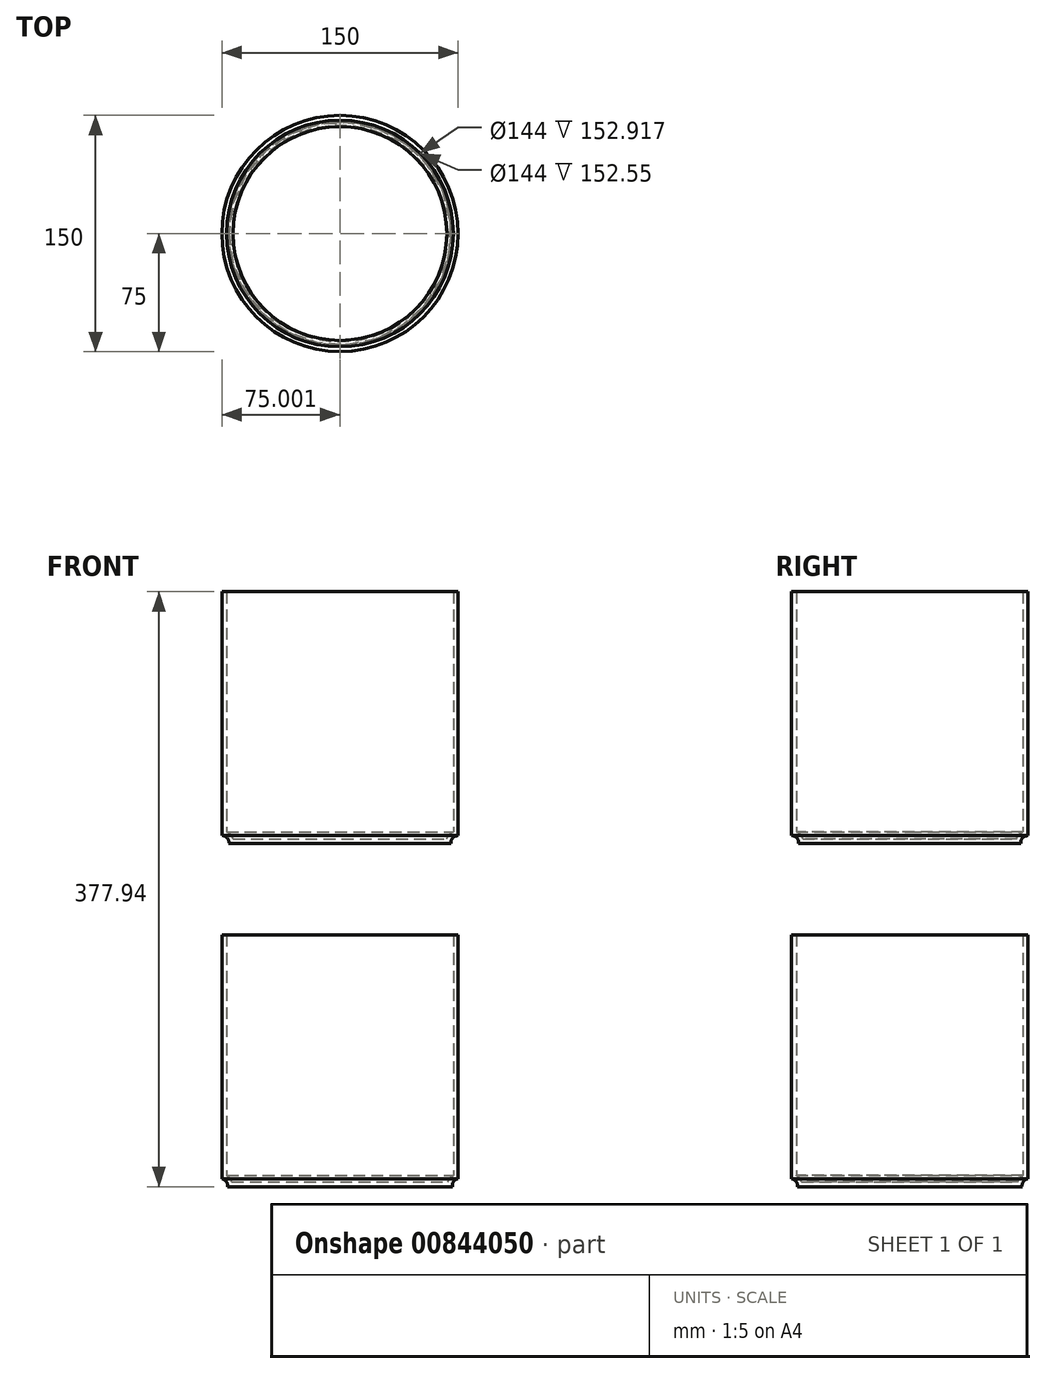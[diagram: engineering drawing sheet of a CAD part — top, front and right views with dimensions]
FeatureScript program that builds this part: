
annotation { "Feature Type Name" : "Feature", "Feature Type Description" : "" }
export const myFeature = defineFeature(function(context is Context, id is Id, definition is map)
    precondition{}
    {
        {
            var Q0;
            Q0=qCreatedBy(makeId("Front.planeOp"),FACE);
            var sketch = newSketch(context, id + "F0", { "sketchPlane" : qUnion([Q0])});
            skLineSegment(sketch, "E0", {"start": v(-217.9, 94.24) * mm, "end": v(-217.9, -60.76) * mm});
            skLineSegment(sketch, "E1", {"start": v(-222.3, -65.76) * mm, "end": v(-292.9, -65.76) * mm});
            skLineSegment(sketch, "E2", {"start": v(-292.9, -65.76) * mm, "end": v(-292.9, 94.24) * mm});
            skLineSegment(sketch, "E3", {"start": v(-292.9, 94.24) * mm, "end": v(-217.9, 94.24) * mm});
            skArc(sketch, "E4", {"start": v(-217.9, -60.76) * mm, "mid": v(-221.3, -62.2) * mm, "end": v(-222.3, -65.76) * mm});
            skLineSegment(sketch, "E5", {"start": v(-217.9, 94.24) * mm, "end": v(-113.07, 94.24) * mm});
            skLineSegment(sketch, "E6", {"start": v(-113.07, 94.24) * mm, "end": v(-113.07, -100.34) * mm});
            skLineSegment(sketch, "E7", {"start": v(-113.07, -100.34) * mm, "end": v(-292.9, -100.34) * mm});
            skLineSegment(sketch, "E8", {"start": v(-292.9, -100.34) * mm, "end": v(-292.9, -65.76) * mm});
            skLineSegment(sketch, "E9", {"start": v(-217.9, -123.7) * mm, "end": v(-217.9, -278.7) * mm});
            skLineSegment(sketch, "E10", {"start": v(-221.48, -283.7) * mm, "end": v(-292.9, -283.7) * mm});
            skLineSegment(sketch, "E11", {"start": v(-292.9, -283.7) * mm, "end": v(-292.9, -123.7) * mm});
            skLineSegment(sketch, "E12", {"start": v(-292.9, -123.7) * mm, "end": v(-217.9, -123.7) * mm});
            skArc(sketch, "E13", {"start": v(-217.9, -278.7) * mm, "mid": v(-220.75, -280.44) * mm, "end": v(-221.48, -283.7) * mm});
            skLineSegment(sketch, "E14", {"start": v(-217.9, -123.7) * mm, "end": v(-112.36, -123.7) * mm});
            skLineSegment(sketch, "E15", {"start": v(-112.36, -123.7) * mm, "end": v(-112.36, -313.53) * mm});
            skLineSegment(sketch, "E16", {"start": v(-112.36, -313.53) * mm, "end": v(-292.9, -313.53) * mm});
            skLineSegment(sketch, "E17", {"start": v(-292.9, -313.53) * mm, "end": v(-292.9, -283.7) * mm});
            skSolve(sketch);
        }
        {
            var Q0;
            Q0=makeQuery(id+"F0.imprint","IMPRINT",FACE,{"disambiguationData":[TD([[makeQuery(id+"F0.imprint","IMPRINT",EDGE,{"derivedFrom":sQuery(id+"F0.wireOp",EDGE,"E0")}),-1.0]])]});
            var Q1;
            Q1=sQuery(id+"F0.wireOp",EDGE,"E2");
            var Q2;
            Q2=sQuery(id+"F0.wireOp",EDGE,"E2");
            revolve(context, id + "F1", {"surfaceOperationType" : NewSurfaceOperationType.NEW, "entities" : qUnion([Q0]), "surfaceEntities" : qUnion([Q1]), "axis" : qUnion([Q2]), "revolveType" : RevolveType.FULL});
        }
        {
            var Q0;
            Q0=makeQuery(id+"F1.opRevolve","SWEPT_FACE",FACE,{"disambiguationData":[OSD([sQuery(id+"F0.wireOp",EDGE,"E3")])]});
            shell(context, id + "F2", {"entities" : qUnion([Q0]), "thickness" : 3 * mm});
        }
        {
            var Q0;
            Q0=makeQuery(id+"F0.imprint","IMPRINT",FACE,{"disambiguationData":[TD([[makeQuery(id+"F0.imprint","IMPRINT",EDGE,{"derivedFrom":sQuery(id+"F0.wireOp",EDGE,"E9")}),-1.0]])]});
            var Q1;
            Q1=sQuery(id+"F0.wireOp",EDGE,"E11");
            var Q2;
            Q2=sQuery(id+"F0.wireOp",EDGE,"E11");
            revolve(context, id + "F3", {"surfaceOperationType" : NewSurfaceOperationType.NEW, "entities" : qUnion([Q0]), "surfaceEntities" : qUnion([Q1]), "axis" : qUnion([Q2]), "revolveType" : RevolveType.FULL});
        }
        {
            var Q0;
            Q0=makeQuery(id+"F3.opRevolve","SWEPT_FACE",FACE,{"disambiguationData":[OSD([sQuery(id+"F0.wireOp",EDGE,"E12")])]});
            shell(context, id + "F4", {"entities" : qUnion([Q0]), "thickness" : 3 * mm});
        }
    });
